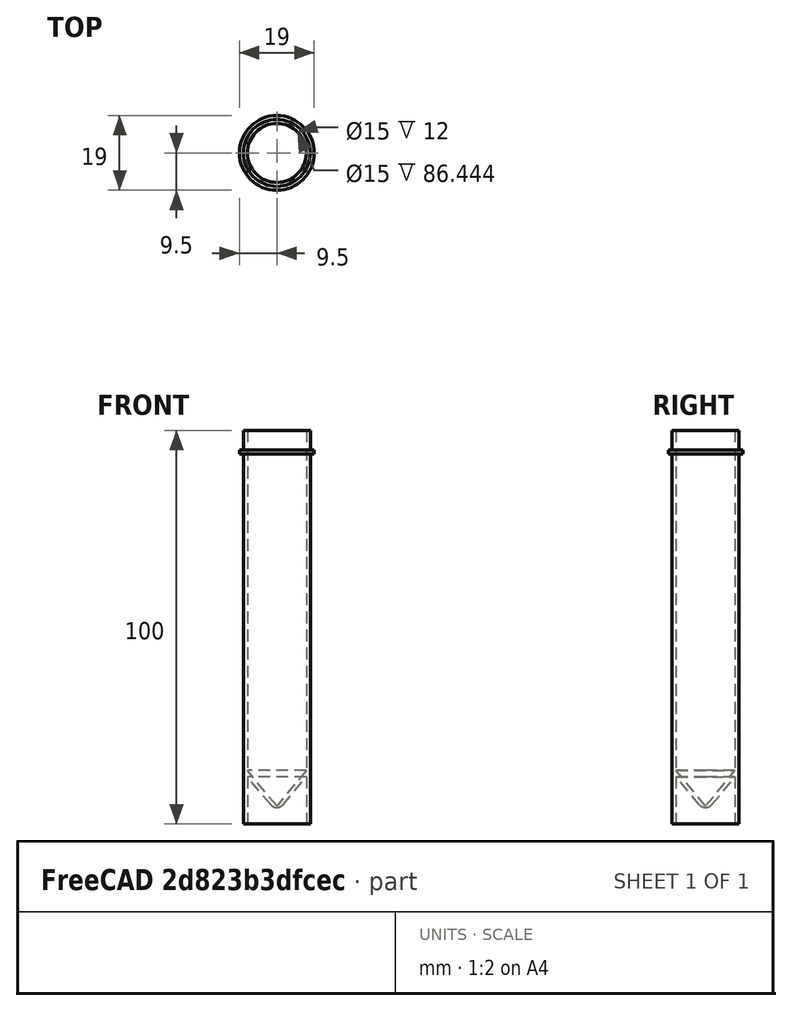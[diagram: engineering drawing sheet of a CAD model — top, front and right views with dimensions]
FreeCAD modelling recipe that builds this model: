
FCSTD DOCUMENT  (FreeCAD 1.0R38641 +678 (Git))
Label: testube
License: All rights reserved
LicenseURL: https://en.wikipedia.org/wiki/All_rights_reserved
objects: Sketcher::SketchObject×1, PartDesign::Revolution×1, PartDesign::Body×1
note: 6 computed .brp shape members not serialized (recipe doc carries the construction recipe); baked Part::Feature solids carry a one-line shape summary decoded from their .brp

FEATURE [Sketcher::SketchObject] Sketch
  ArcFitTolerance = 1e-06
  AttachmentSupport = -> [XZ_Plane]
  FullyConstrained = true
  MakeInternals = false
  MapMode = 5
  Placement = pos=(0,0,0) rot=(1,0,0;1.5708rad)
  sketch-geometry (13):
    g0: LineSegment StartX=8.5 StartY=94 StartZ=0 EndX=9.5 EndY=94 EndZ=0
    g1: LineSegment StartX=9.5 StartY=94 StartZ=0 EndX=9.5 EndY=95 EndZ=0
    g2: LineSegment StartX=9.5 StartY=95 StartZ=0 EndX=8.5 EndY=95 EndZ=0
    g3: LineSegment StartX=8.5 StartY=95 StartZ=0 EndX=8.5 EndY=100 EndZ=0
    g4: LineSegment StartX=8.5 StartY=100 StartZ=0 EndX=7.5 EndY=100 EndZ=0
    g5: LineSegment StartX=7.5 StartY=100 StartZ=0 EndX=7.5 EndY=13.5557 EndZ=0
    g6: LineSegment StartX=7.5 StartY=13.5557 StartZ=0 EndX=9e-16 EndY=4.61757 EndZ=0
    g7: LineSegment StartX=1.53209 StartY=4.88772 StartZ=0 EndX=7.5 EndY=12 EndZ=0
    g8: LineSegment StartX=7.5 StartY=12 StartZ=0 EndX=7.5 EndY=0 EndZ=0
    g9: LineSegment StartX=7.5 StartY=0 StartZ=0 EndX=8.5 EndY=0 EndZ=0
    g10: LineSegment StartX=8.5 StartY=0 StartZ=0 EndX=8.5 EndY=94 EndZ=0
    g11: ArcOfCircle CenterX=0 CenterY=6.1733 CenterZ=0 NormalX=0 NormalY=0 NormalZ=1 AngleXU=0 Radius=2 StartAngle=4.71239 EndAngle=5.58505
    g12: LineSegment StartX=-4e-16 StartY=4.1733 StartZ=0 EndX=9e-16 EndY=4.61757 EndZ=0
  constraints (39):
    c: Horizontal(g0)
    c: Coincident(g0,g1)
    c: Coincident(g1,g2)
    c: Coincident(g2,g3)
    c: Vertical(g3)
    c: Coincident(g3,g4)
    c: Coincident(g4,g5)
    c: Vertical(g5)
    c: Coincident(g5,g6)
    c: Coincident(g7,g8)
    c: Coincident(g8,g9)
    c: Horizontal(g9)
    c: Coincident(g9,g10)
    c: Coincident(g10,g0)
    c: Vertical(g10)
    c: Horizontal(g4)
    c: Vertical(g2,g0)
    c: Vertical(g1)
    c: Horizontal(g2)
    c: PointOnObject(g9,g-1)
    c: Vertical(g8)
    c: Vertical(g7,g5)
    c: Parallel(g6,g7)
    c: PointOnObject(g11,g-2)
    c: Tangent(g11,g7) = -1.5708
    c: PointOnObject(g6,g-2)
    c: Distance(g9,g9) = 1
    c: Distance(g6,g7) = 1
    c: Radius(g11) = 2
    c: Distance(g1,g1) = 1
    c: Distance(g3,g3) = 5
    c: DistanceY(g9,g3) = 100
    c: Coincident(g12,g6)
    c: Distance(g0,g0) = 1
    c: Distance(g3,g-2) = 8.5
    c: PointOnObject(g12,g-2)
    c: Coincident(g12,g11)
    c: DistanceY(g8,g8) = 12
    c: Angle(g-1,g7) = 0.872665
FEATURE [PartDesign::Revolution] Revolution
  Angle = 360
  Angle2 = 60
  Axis = (0,2e-16,1)
  Base = (0,0,0)
  Placement = pos=(0,0,0) rot=(1,0,0;1.5708rad)
  Profile = -> Sketch
  ReferenceAxis = -> Sketch [V_Axis]
  Refine = true
  Reversed = true
  Suppressed = false
  Type = 0
FEATURE [PartDesign::Body] Body  label="testube"
  AllowCompound = false
  Group = -> [Sketch,Revolution]
  Origin = -> Origin
  Tip = -> Revolution
